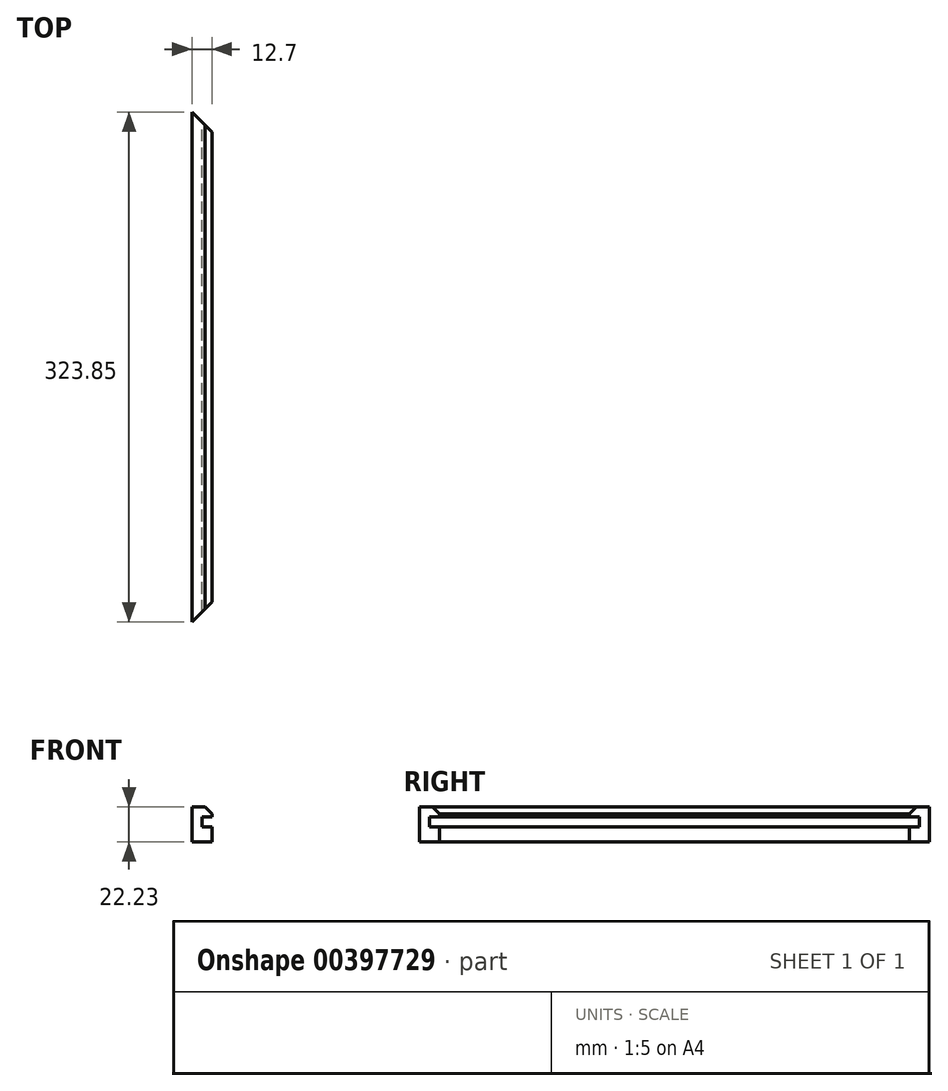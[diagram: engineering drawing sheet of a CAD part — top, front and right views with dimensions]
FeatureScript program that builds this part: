
annotation { "Feature Type Name" : "Feature", "Feature Type Description" : "" }
export const myFeature = defineFeature(function(context is Context, id is Id, definition is map)
    precondition{}
    {
        {
            var Q0;
            Q0=qCreatedBy(makeId("Front.planeOp"),FACE);
            var sketch = newSketch(context, id + "F0", { "sketchPlane" : qUnion([Q0])});
            skLineSegment(sketch, "E0.bottom", {"start": v(0, 0) * mm, "end": v(12.7, 0) * mm});
            skLineSegment(sketch, "E0.top", {"start": v(0, 22.23) * mm, "end": v(8.2, 22.22) * mm});
            skLineSegment(sketch, "E0.left", {"start": v(0, 0) * mm, "end": v(0, 22.23) * mm});
            skLineSegment(sketch, "E0.right", {"start": v(12.7, 0) * mm, "end": v(12.7, 9.52) * mm});
            skLineSegment(sketch, "E1.bottom", {"start": v(12.7, 15.88) * mm, "end": v(6.35, 15.88) * mm});
            skLineSegment(sketch, "E1.top", {"start": v(12.7, 9.52) * mm, "end": v(6.35, 9.52) * mm});
            skLineSegment(sketch, "E1.right", {"start": v(6.35, 15.88) * mm, "end": v(6.35, 9.52) * mm});
            skLineSegment(sketch, "E2.trimOffspring", {"start": v(12.7, 15.88) * mm, "end": v(12.7, 17.73) * mm});
            skLineSegment(sketch, "E3", {"start": v(12.7, 17.73) * mm, "end": v(8.2, 22.22) * mm});
            skSolve(sketch);
        }
        {
            var Q0;
            Q0=makeQuery(id+"F0.imprint","IMPRINT",FACE,{"disambiguationData":[TD([[makeQuery(id+"F0.imprint","IMPRINT",EDGE,{"derivedFrom":sQuery(id+"F0.wireOp",EDGE,"E0.bottom")}),1.0]])]});
            extrude(context, id + "F1", {"entities" : qUnion([Q0]), "depth" : 323.85 * mm});
        }
        {
            var Q0;
            Q0=makeQuery(id+"F1.opExtrude","SWEPT_FACE",FACE,{"disambiguationData":[OSD([sQuery(id+"F0.wireOp",EDGE,"E0.bottom")])]});
            var sketch = newSketch(context, id + "F2", { "sketchPlane" : qUnion([Q0])});
            skLineSegment(sketch, "E4", {"start": v(0, 323.85) * mm, "end": v(12.7, 311.15) * mm});
            skLineSegment(sketch, "E5", {"start": v(12.7, 311.15) * mm, "end": v(12.7, 323.85) * mm});
            skLineSegment(sketch, "E6", {"start": v(12.7, 323.85) * mm, "end": v(0, 323.85) * mm});
            skLineSegment(sketch, "E7", {"start": v(0, 0) * mm, "end": v(12.7, 12.7) * mm});
            skLineSegment(sketch, "E8", {"start": v(12.7, 12.7) * mm, "end": v(12.7, 0) * mm});
            skLineSegment(sketch, "E9", {"start": v(12.7, 0) * mm, "end": v(0, 0) * mm});
            skSolve(sketch);
        }
        {
            var Q0;
            Q0=makeQuery(id+"F2.imprint","IMPRINT",FACE,{"disambiguationData":[TD([[makeQuery(id+"F2.imprint","IMPRINT",EDGE,{"derivedFrom":sQuery(id+"F2.wireOp",EDGE,"E4")}),1.0]])]});
            var Q1;
            Q1=makeQuery(id+"F2.imprint","IMPRINT",FACE,{"disambiguationData":[TD([[makeQuery(id+"F2.imprint","IMPRINT",EDGE,{"derivedFrom":sQuery(id+"F2.wireOp",EDGE,"E7")}),-1.0]])]});
            extrude(context, id + "F3", {"entities" : qUnion([Q0, Q1]), "operationType" : NewBodyOperationType.REMOVE, "endBound" : BoundingType.THROUGH_ALL, "oppositeDirection" : true, "depth" : 25.4 * mm});
        }
    });
